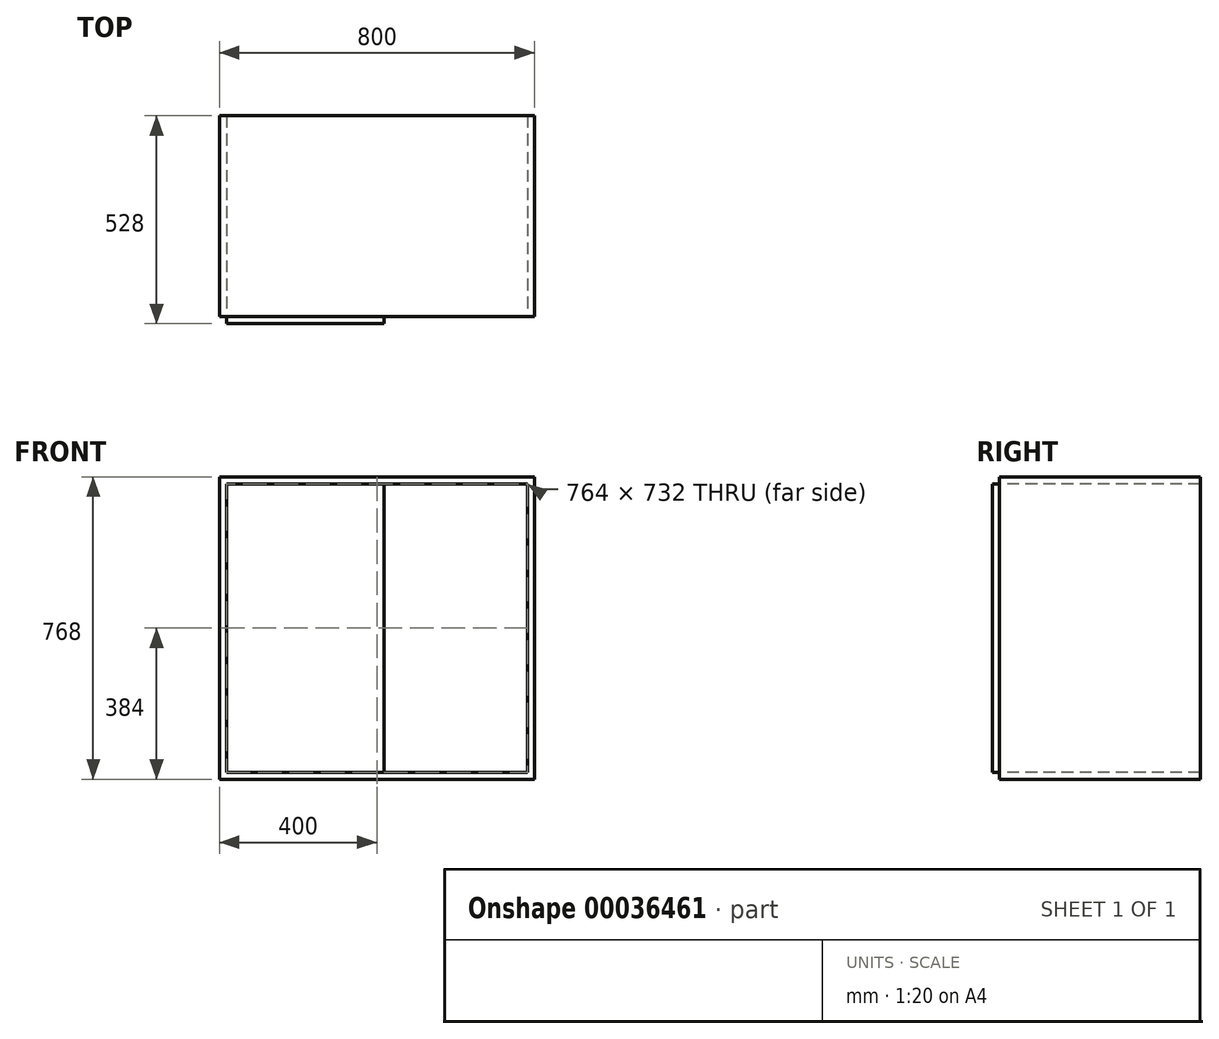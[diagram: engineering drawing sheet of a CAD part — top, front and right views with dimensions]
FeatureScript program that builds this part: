
annotation { "Feature Type Name" : "Feature", "Feature Type Description" : "" }
export const myFeature = defineFeature(function(context is Context, id is Id, definition is map)
    precondition{}
    {
        {
            var Q0;
            Q0=qCreatedBy(makeId("Top.planeOp"),FACE);
            var sketch = newSketch(context, id + "F0", { "sketchPlane" : qUnion([Q0])});
            skLineSegment(sketch, "E0.rect.bottom", {"start": v(-400, -255) * mm, "end": v(400, -255) * mm});
            skLineSegment(sketch, "E0.rect.top", {"start": v(-400, 255) * mm, "end": v(400, 255) * mm});
            skLineSegment(sketch, "E0.rect.left", {"start": v(-400, -255) * mm, "end": v(-400, 255) * mm});
            skLineSegment(sketch, "E0.rect.right", {"start": v(400, -255) * mm, "end": v(400, 255) * mm});
            skPoint(sketch, "E0.rect.middle", {"position": v(0, 0) * mm});
            skSolve(sketch);
        }
        {
            var Q0;
            Q0=makeQuery(id+"F0.imprint","IMPRINT",FACE,{"disambiguationData":[TD([[makeQuery(id+"F0.imprint","IMPRINT",EDGE,{"derivedFrom":sQuery(id+"F0.wireOp",EDGE,"E0.rect.bottom")}),1.0]])]});
            extrude(context, id + "F1", {"entities" : qUnion([Q0]), "depth" : 18 * mm});
        }
        {
            var Q0;
            Q0=makeQuery(id+"F1.opExtrude","CAP_FACE",FACE,{"disambiguationData":[OSD([sQuery(id+"F0.wireOp",EDGE,"E0.rect.bottom"),sQuery(id+"F0.wireOp",EDGE,"E0.rect.top"),sQuery(id+"F0.wireOp",EDGE,"E0.rect.left"),sQuery(id+"F0.wireOp",EDGE,"E0.rect.right")])],"isStart":false});
            var sketch = newSketch(context, id + "F2", { "sketchPlane" : qUnion([Q0])});
            skLineSegment(sketch, "E1.bottom", {"start": v(-400, 255) * mm, "end": v(-382, 255) * mm});
            skLineSegment(sketch, "E1.top", {"start": v(-400, -255) * mm, "end": v(-382, -255) * mm});
            skLineSegment(sketch, "E1.left", {"start": v(-400, 255) * mm, "end": v(-400, -255) * mm});
            skLineSegment(sketch, "E1.right", {"start": v(-382, 255) * mm, "end": v(-382, -255) * mm});
            skSolve(sketch);
        }
        {
            var Q0;
            Q0=makeQuery(id+"F2.imprint","IMPRINT",FACE,{"disambiguationData":[TD([[makeQuery(id+"F2.imprint","IMPRINT",EDGE,{"derivedFrom":sQuery(id+"F2.wireOp",EDGE,"E1.bottom")}),-1.0]])]});
            extrude(context, id + "F3", {"entities" : qUnion([Q0]), "operationType" : NewBodyOperationType.ADD, "depth" : 750 * mm});
        }
        {
            var Q0;
            Q0=makeQuery(id+"F1.opExtrude","CAP_FACE",FACE,{"disambiguationData":[OSD([sQuery(id+"F0.wireOp",EDGE,"E0.rect.bottom"),sQuery(id+"F0.wireOp",EDGE,"E0.rect.top"),sQuery(id+"F0.wireOp",EDGE,"E0.rect.left"),sQuery(id+"F0.wireOp",EDGE,"E0.rect.right")])],"isStart":false});
            var sketch = newSketch(context, id + "F4", { "sketchPlane" : qUnion([Q0])});
            skLineSegment(sketch, "E2.bottom", {"start": v(400, 255) * mm, "end": v(382, 255) * mm});
            skLineSegment(sketch, "E2.top", {"start": v(400, -255) * mm, "end": v(382, -255) * mm});
            skLineSegment(sketch, "E2.left", {"start": v(400, 255) * mm, "end": v(400, -255) * mm});
            skLineSegment(sketch, "E2.right", {"start": v(382, 255) * mm, "end": v(382, -255) * mm});
            skSolve(sketch);
        }
        {
            var Q0;
            Q0=makeQuery(id+"F4.imprint","IMPRINT",FACE,{"disambiguationData":[TD([[makeQuery(id+"F4.imprint","IMPRINT",EDGE,{"derivedFrom":sQuery(id+"F4.wireOp",EDGE,"E2.bottom")}),-1.0]])]});
            extrude(context, id + "F5", {"entities" : qUnion([Q0]), "operationType" : NewBodyOperationType.ADD, "depth" : 750 * mm});
        }
        {
            var Q0;
            Q0=makeQuery(id+"F5.opExtrude","SWEPT_FACE",FACE,{"disambiguationData":[OSD([sQuery(id+"F4.wireOp",EDGE,"E2.right")])]});
            var sketch = newSketch(context, id + "F6", { "sketchPlane" : qUnion([Q0])});
            skLineSegment(sketch, "E3.bottom", {"start": v(-255, 768) * mm, "end": v(255, 768) * mm});
            skLineSegment(sketch, "E3.top", {"start": v(-255, 750) * mm, "end": v(255, 750) * mm});
            skLineSegment(sketch, "E3.left", {"start": v(-255, 768) * mm, "end": v(-255, 750) * mm});
            skLineSegment(sketch, "E3.right", {"start": v(255, 768) * mm, "end": v(255, 750) * mm});
            skSolve(sketch);
        }
        {
            var Q0;
            Q0=makeQuery(id+"F6.imprint","IMPRINT",FACE,{"disambiguationData":[TD([[makeQuery(id+"F6.imprint","IMPRINT",EDGE,{"derivedFrom":sQuery(id+"F6.wireOp",EDGE,"E3.bottom")}),-1.0]])]});
            extrude(context, id + "F7", {"entities" : qUnion([Q0]), "operationType" : NewBodyOperationType.ADD, "depth" : 764 * mm});
        }
        {
            var Q0;
            Q0=makeQuery(id+"F7.boolean.opBoolean","MERGE",FACE,{"derivedFrom":[makeQuery(id+"F5.boolean.opBoolean","MERGE",FACE,{"derivedFrom":[makeQuery(id+"F3.boolean.opBoolean","MERGE",FACE,{"derivedFrom":[makeQuery(id+"F1.opExtrude","SWEPT_FACE",FACE,{"disambiguationData":[OSD([sQuery(id+"F0.wireOp",EDGE,"E0.rect.bottom")])]}),makeQuery(id+"F3.opExtrude","SWEPT_FACE",FACE,{"disambiguationData":[OSD([sQuery(id+"F2.wireOp",EDGE,"E1.top")])]})]}),makeQuery(id+"F5.opExtrude","SWEPT_FACE",FACE,{"disambiguationData":[OSD([sQuery(id+"F4.wireOp",EDGE,"E2.top")])]})]}),makeQuery(id+"F7.opExtrude","SWEPT_FACE",FACE,{"disambiguationData":[OSD([sQuery(id+"F6.wireOp",EDGE,"E3.right")])]})]});
            var sketch = newSketch(context, id + "F8", { "sketchPlane" : qUnion([Q0])});
            skLineSegment(sketch, "E4.bottom", {"start": v(18, 768) * mm, "end": v(-382, 768) * mm});
            skLineSegment(sketch, "E4.top", {"start": v(18, 0) * mm, "end": v(-382, 0) * mm});
            skLineSegment(sketch, "E4.left", {"start": v(18, 768) * mm, "end": v(18, 0) * mm});
            skLineSegment(sketch, "E4.right", {"start": v(-382, 768) * mm, "end": v(-382, 0) * mm});
            skSolve(sketch);
        }
        {
            var Q0;
            {var subQ0=sQuery(id+"F0.wireOp",EDGE,"E0.rect.bottom");var subQ4=sQuery(id+"F8.wireOp",EDGE,"E4.right");var subQ6=makeQuery(id+"F1.opExtrude","CAP_EDGE",EDGE,{"disambiguationData":[OSD([subQ0])],"isStart":false});var subQ8=makeQuery(id+"F8.imprint","INTERSECT",VERTEX,{"derivedFrom":[subQ6,subQ4]});Q0=makeQuery(id+"F8.imprint","IMPRINT",FACE,{"disambiguationData":[TD([[makeQuery(id+"F8.imprint","IMPRINT",EDGE,{"disambiguationData":[TD([[subQ8,-1.0]])],"derivedFrom":subQ6}),1.0]])]});}
            extrude(context, id + "F9", {"entities" : qUnion([Q0]), "operationType" : NewBodyOperationType.ADD, "depth" : 18 * mm});
        }
    });
